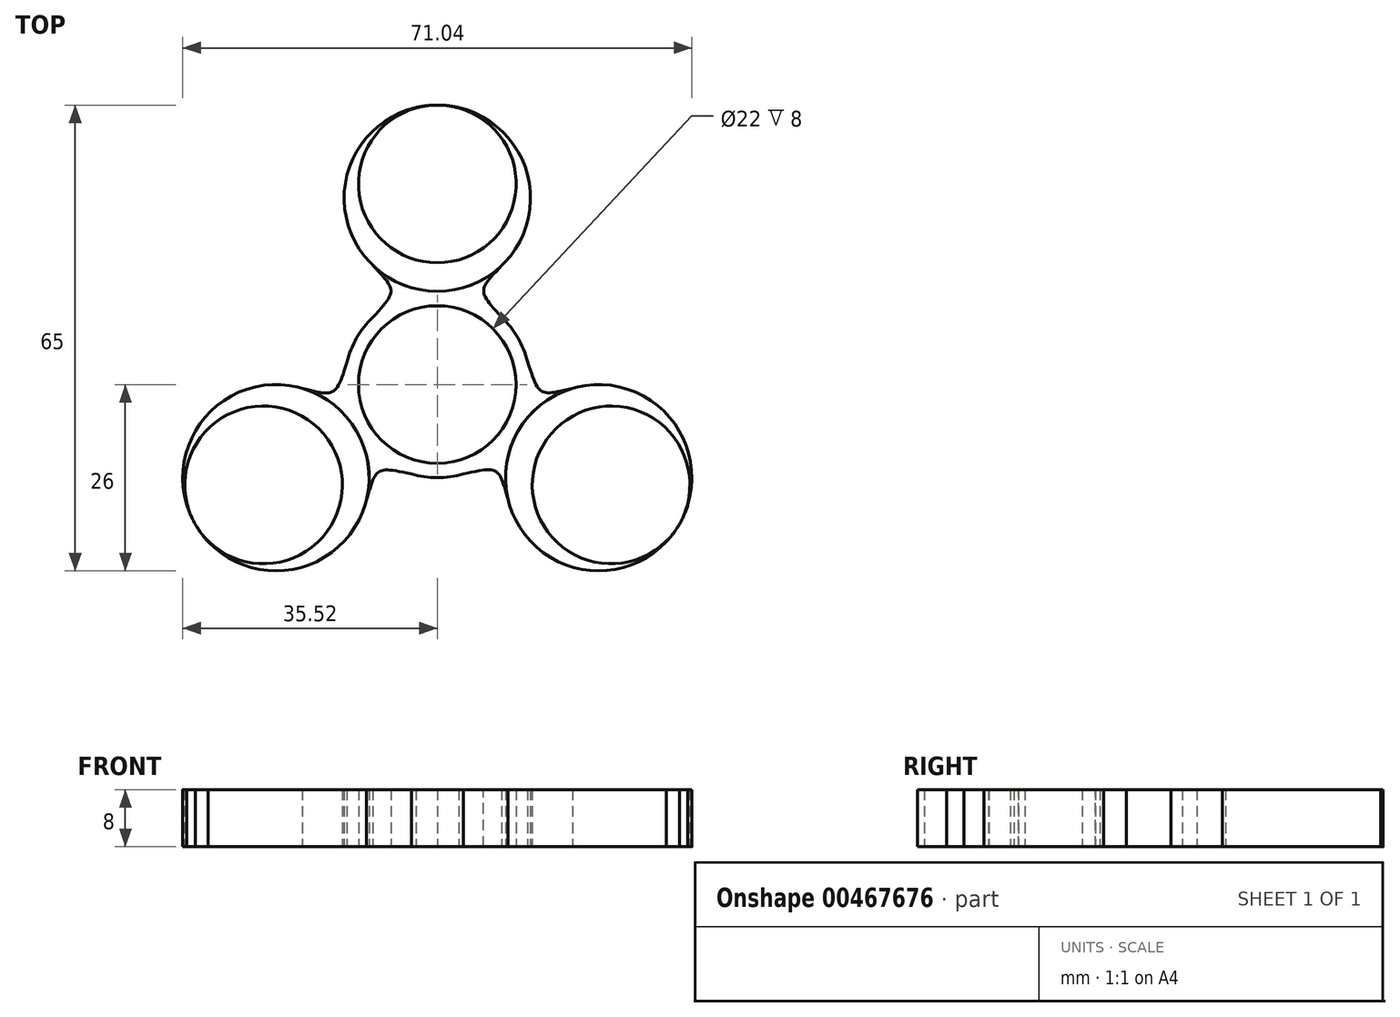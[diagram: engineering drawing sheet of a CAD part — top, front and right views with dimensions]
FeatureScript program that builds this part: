
annotation { "Feature Type Name" : "Feature", "Feature Type Description" : "" }
export const myFeature = defineFeature(function(context is Context, id is Id, definition is map)
    precondition{}
    {
        {
            var Q0;
            Q0=qCreatedBy(makeId("Top.planeOp"),FACE);
            var sketch = newSketch(context, id + "F0", { "sketchPlane" : qUnion([Q0])});
            skLineSegment(sketch, "E0", {"start": v(0, 0) * mm, "end": v(0, 28) * mm, "construction": true});
            skCircle(sketch, "E1", {"center": v(0, 28) * mm, "radius": 11 * mm});
            skLineSegment(sketch, "E2", {"start": v(0, 0) * mm, "end": v(0, 26) * mm, "construction": true});
            skCircle(sketch, "E3", {"center": v(0, 26) * mm, "radius": 13 * mm});
            skCircle(sketch, "E4", {"center": v(0, 0) * mm, "radius": 11 * mm});
            skCircle(sketch, "E5.0", {"center": v(0, 0) * mm, "radius": 13 * mm});
            skLineSegment(sketch, "E6.bottom", {"start": v(-3, 41.5) * mm, "end": v(3, 41.5) * mm});
            skLineSegment(sketch, "E6.top", {"start": v(-3, 36.5) * mm, "end": v(3, 36.5) * mm});
            skLineSegment(sketch, "E6.left", {"start": v(-3, 41.5) * mm, "end": v(-3, 36.5) * mm});
            skLineSegment(sketch, "E6.right", {"start": v(3, 41.5) * mm, "end": v(3, 36.5) * mm});
            skPoint(sketch, "E6.middle", {"position": v(0, 39) * mm});
            skFitSpline(sketch, "E7", {"points": [v(-8.98, 16.6) * mm, v(-9, 9.39) * mm], "startDerivative": vector(10.1, -10.51) * mm, "endDerivative": vector(-10.14, -11.12) * mm});
            skFitSpline(sketch, "E8.MirrorCS", {"points": [v(8.98, 16.6) * mm, v(9, 9.39) * mm], "startDerivative": vector(-10.1, -10.51) * mm, "endDerivative": vector(10.14, -11.12) * mm});
            skCircle(sketch, "E9.1.0", {"center": v(-22.52, -13) * mm, "radius": 13 * mm});
            skLineSegment(sketch, "E9.1.1", {"start": v(-37.44, -18.15) * mm, "end": v(-33.1, -15.65) * mm});
            skPoint(sketch, "E9.1.2", {"position": v(-33.77, -19.5) * mm});
            skLineSegment(sketch, "E9.1.3", {"start": v(-34.44, -23.35) * mm, "end": v(-30.1, -20.85) * mm});
            skLineSegment(sketch, "E9.1.4", {"start": v(-34.44, -23.35) * mm, "end": v(-37.44, -18.15) * mm});
            skCircle(sketch, "E9.1.5", {"center": v(-24.25, -14) * mm, "radius": 11 * mm});
            skLineSegment(sketch, "E9.1.6", {"start": v(-30.1, -20.85) * mm, "end": v(-33.1, -15.65) * mm});
            skCircle(sketch, "E9.2.0", {"center": v(22.52, -13) * mm, "radius": 13 * mm});
            skLineSegment(sketch, "E9.2.1", {"start": v(34.44, -23.35) * mm, "end": v(30.1, -20.85) * mm});
            skPoint(sketch, "E9.2.2", {"position": v(33.77, -19.5) * mm});
            skLineSegment(sketch, "E9.2.3", {"start": v(37.44, -18.15) * mm, "end": v(33.1, -15.65) * mm});
            skLineSegment(sketch, "E9.2.4", {"start": v(37.44, -18.15) * mm, "end": v(34.44, -23.35) * mm});
            skCircle(sketch, "E9.2.5", {"center": v(24.25, -14) * mm, "radius": 11 * mm});
            skLineSegment(sketch, "E9.2.6", {"start": v(33.1, -15.65) * mm, "end": v(30.1, -20.85) * mm});
            skFitSpline(sketch, "E10", {"points": [v(18.87, -0.52) * mm, v(12.6, 3.2) * mm], "startDerivative": vector(-14.16, -3.5) * mm, "endDerivative": vector(-4.56, 14.34) * mm});
            skFitSpline(sketch, "E11.MirrorCS", {"points": [v(9.86, -15.98) * mm, v(3.64, -12.48) * mm], "startDerivative": vector(-4.05, 14) * mm, "endDerivative": vector(-14.7, -3.22) * mm});
            skFitSpline(sketch, "E12", {"points": [v(-9.89, -16.08) * mm, v(-3.63, -12.48) * mm], "startDerivative": vector(4.05, 14) * mm, "endDerivative": vector(14.7, -3.22) * mm});
            skFitSpline(sketch, "E13.MirrorCS", {"points": [v(-18.86, -0.52) * mm, v(-12.63, 3.1) * mm], "startDerivative": vector(14.16, -3.5) * mm, "endDerivative": vector(4.56, 14.34) * mm});
            skSolve(sketch);
        }
        {
            var Q0;
            {var subQ4=sQuery(id+"F0.wireOp",EDGE,"E1");Q0=makeQuery(id+"F0.imprint","IMPRINT",FACE,{"disambiguationData":[TD([[makeQuery(id+"F0.imprint","IMPRINT",EDGE,{"derivedFrom":subQ4}),-1.0]])]});}
            var Q1;
            {var subQ2=sQuery(id+"F0.wireOp",EDGE,"E9.2.5");Q1=makeQuery(id+"F0.imprint","IMPRINT",FACE,{"disambiguationData":[TD([[makeQuery(id+"F0.imprint","IMPRINT",EDGE,{"derivedFrom":subQ2}),-1.0]])]});}
            var Q2;
            Q2=makeQuery(id+"F0.imprint","IMPRINT",FACE,{"disambiguationData":[TD([[makeQuery(id+"F0.imprint","IMPRINT",EDGE,{"derivedFrom":sQuery(id+"F0.wireOp",EDGE,"E4")}),-1.0]])]});
            var Q3;
            {var subQ2=sQuery(id+"F0.wireOp",EDGE,"E9.1.5");Q3=makeQuery(id+"F0.imprint","IMPRINT",FACE,{"disambiguationData":[TD([[makeQuery(id+"F0.imprint","IMPRINT",EDGE,{"derivedFrom":subQ2}),-1.0]])]});}
            var Q4;
            {var subQ0=sQuery(id+"F0.wireOp",EDGE,"E7");Q4=makeQuery(id+"F0.imprint","IMPRINT",FACE,{"disambiguationData":[TD([[makeQuery(id+"F0.imprint","IMPRINT",EDGE,{"derivedFrom":subQ0}),1.0]])]});}
            var Q5;
            {var subQ0=sQuery(id+"F0.wireOp",EDGE,"E8.MirrorCS");Q5=makeQuery(id+"F0.imprint","IMPRINT",FACE,{"disambiguationData":[TD([[makeQuery(id+"F0.imprint","IMPRINT",EDGE,{"derivedFrom":subQ0}),-1.0]])]});}
            var Q6;
            {var subQ0=sQuery(id+"F0.wireOp",EDGE,"E13.MirrorCS");Q6=makeQuery(id+"F0.imprint","IMPRINT",FACE,{"disambiguationData":[TD([[makeQuery(id+"F0.imprint","IMPRINT",EDGE,{"derivedFrom":subQ0}),-1.0]])]});}
            var Q7;
            {var subQ0=sQuery(id+"F0.wireOp",EDGE,"E12");Q7=makeQuery(id+"F0.imprint","IMPRINT",FACE,{"disambiguationData":[TD([[makeQuery(id+"F0.imprint","IMPRINT",EDGE,{"derivedFrom":subQ0}),1.0]])]});}
            var Q8;
            {var subQ0=sQuery(id+"F0.wireOp",EDGE,"E11.MirrorCS");Q8=makeQuery(id+"F0.imprint","IMPRINT",FACE,{"disambiguationData":[TD([[makeQuery(id+"F0.imprint","IMPRINT",EDGE,{"derivedFrom":subQ0}),-1.0]])]});}
            var Q9;
            {var subQ0=sQuery(id+"F0.wireOp",EDGE,"E10");Q9=makeQuery(id+"F0.imprint","IMPRINT",FACE,{"disambiguationData":[TD([[makeQuery(id+"F0.imprint","IMPRINT",EDGE,{"derivedFrom":subQ0}),1.0]])]});}
            extrude(context, id + "F1", {"entities" : qUnion([Q0, Q1, Q2, Q3, Q4, Q5, Q6, Q7, Q8, Q9]), "depth" : 8 * mm, "offsetDistance" : 25 * mm});
        }
        {
            var Q0;
            {var subQ6=sQuery(id+"F0.wireOp",EDGE,"E6.right");var subQ7=sQuery(id+"F0.wireOp",EDGE,"E1");var subQ8=makeQuery(id+"F0.imprint","INTERSECT",VERTEX,{"derivedFrom":[subQ7,subQ6]});Q0=makeQuery(id+"F0.imprint","IMPRINT",FACE,{"disambiguationData":[TD([[makeQuery(id+"F0.imprint","IMPRINT",EDGE,{"disambiguationData":[TD([[subQ8,1.0]])],"derivedFrom":subQ7}),-1.0]])]});}
            var Q1;
            {var subQ0=sQuery(id+"F0.wireOp",EDGE,"E9.1.0");var subQ9=makeQuery(id+"F0.imprint","INTERSECT",VERTEX,{"derivedFrom":[subQ0,sQuery(id+"F0.wireOp",EDGE,"E12")]});Q1=makeQuery(id+"F0.imprint","IMPRINT",FACE,{"disambiguationData":[TD([[makeQuery(id+"F0.imprint","IMPRINT",EDGE,{"disambiguationData":[TD([[subQ9,1.0]])],"derivedFrom":subQ0}),1.0]])]});}
            var Q2;
            {var subQ0=sQuery(id+"F0.wireOp",EDGE,"E9.2.0");var subQ9=makeQuery(id+"F0.imprint","INTERSECT",VERTEX,{"derivedFrom":[subQ0,sQuery(id+"F0.wireOp",EDGE,"E10")]});Q2=makeQuery(id+"F0.imprint","IMPRINT",FACE,{"disambiguationData":[TD([[makeQuery(id+"F0.imprint","IMPRINT",EDGE,{"disambiguationData":[TD([[subQ9,1.0]])],"derivedFrom":subQ0}),1.0]])]});}
            extrude(context, id + "F2", {"entities" : qUnion([Q0, Q1, Q2]), "depth" : 8 * mm, "offsetDistance" : 25 * mm});
        }
        {
            var Q0;
            {var subQ4=sQuery(id+"F0.wireOp",EDGE,"E9.1.6");Q0=makeQuery(id+"F0.imprint","IMPRINT",FACE,{"disambiguationData":[TD([[makeQuery(id+"F0.imprint","IMPRINT",EDGE,{"derivedFrom":subQ4}),1.0]])]});}
            var Q1;
            {var subQ0=sQuery(id+"F0.wireOp",EDGE,"E9.1.4");Q1=makeQuery(id+"F0.imprint","IMPRINT",FACE,{"disambiguationData":[TD([[makeQuery(id+"F0.imprint","IMPRINT",EDGE,{"derivedFrom":subQ0}),-1.0]])]});}
            var Q2;
            {var subQ0=sQuery(id+"F0.wireOp",EDGE,"E9.2.4");Q2=makeQuery(id+"F0.imprint","IMPRINT",FACE,{"disambiguationData":[TD([[makeQuery(id+"F0.imprint","IMPRINT",EDGE,{"derivedFrom":subQ0}),-1.0]])]});}
            var Q3;
            {var subQ4=sQuery(id+"F0.wireOp",EDGE,"E9.2.6");Q3=makeQuery(id+"F0.imprint","IMPRINT",FACE,{"disambiguationData":[TD([[makeQuery(id+"F0.imprint","IMPRINT",EDGE,{"derivedFrom":subQ4}),1.0]])]});}
            var Q4;
            {var subQ1=sQuery(id+"F0.wireOp",EDGE,"E6.bottom");Q4=makeQuery(id+"F0.imprint","IMPRINT",FACE,{"disambiguationData":[TD([[makeQuery(id+"F0.imprint","IMPRINT",EDGE,{"derivedFrom":subQ1}),-1.0]])]});}
            var Q5;
            {var subQ1=sQuery(id+"F0.wireOp",EDGE,"E6.top");Q5=makeQuery(id+"F0.imprint","IMPRINT",FACE,{"disambiguationData":[TD([[makeQuery(id+"F0.imprint","IMPRINT",EDGE,{"derivedFrom":subQ1}),1.0]])]});}
            extrude(context, id + "F3", {"entities" : qUnion([Q0, Q1, Q2, Q3, Q4, Q5]), "operationType" : NewBodyOperationType.REMOVE, "depth" : 8 * mm, "offsetDistance" : 25 * mm});
        }
    });
